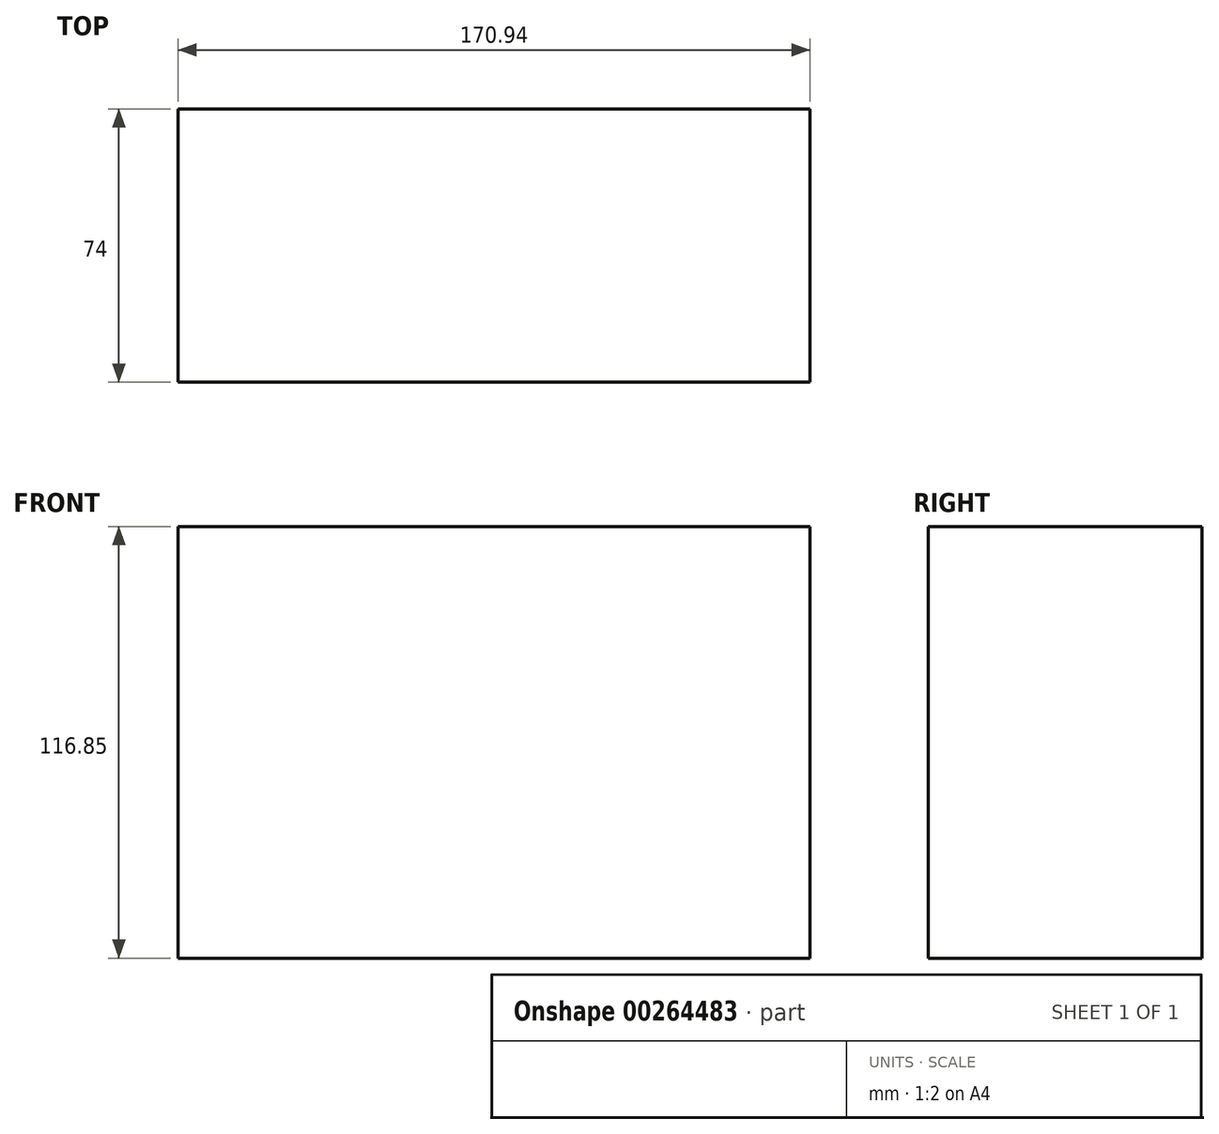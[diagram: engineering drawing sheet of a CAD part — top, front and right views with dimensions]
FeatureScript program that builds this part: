
annotation { "Feature Type Name" : "Feature", "Feature Type Description" : "" }
export const myFeature = defineFeature(function(context is Context, id is Id, definition is map)
    precondition{}
    {
        {
            var Q0;
            Q0=qCreatedBy(makeId("Top.planeOp"),FACE);
            var sketch = newSketch(context, id + "F0", { "sketchPlane" : qUnion([Q0])});
            skLineSegment(sketch, "E0.bottom", {"start": v(-85.48, 37) * mm, "end": v(85.48, 37) * mm});
            skLineSegment(sketch, "E0.top", {"start": v(-85.48, -37) * mm, "end": v(85.48, -37) * mm});
            skLineSegment(sketch, "E0.left", {"start": v(-85.47, 37) * mm, "end": v(-85.48, -37) * mm});
            skLineSegment(sketch, "E0.right", {"start": v(85.48, 37) * mm, "end": v(85.47, -37) * mm});
            skLineSegment(sketch, "E1", {"start": v(0, 37) * mm, "end": v(0, -37) * mm, "construction": true});
            skSolve(sketch);
        }
        {
            var Q0;
            Q0=makeQuery(id+"F0.imprint","IMPRINT",FACE,{"disambiguationData":[TD([[makeQuery(id+"F0.imprint","IMPRINT",EDGE,{"derivedFrom":sQuery(id+"F0.wireOp",EDGE,"E0.bottom")}),-1.0]])]});
            extrude(context, id + "F1", {"entities" : qUnion([Q0]), "depth" : 116.85 * mm});
        }
    });
